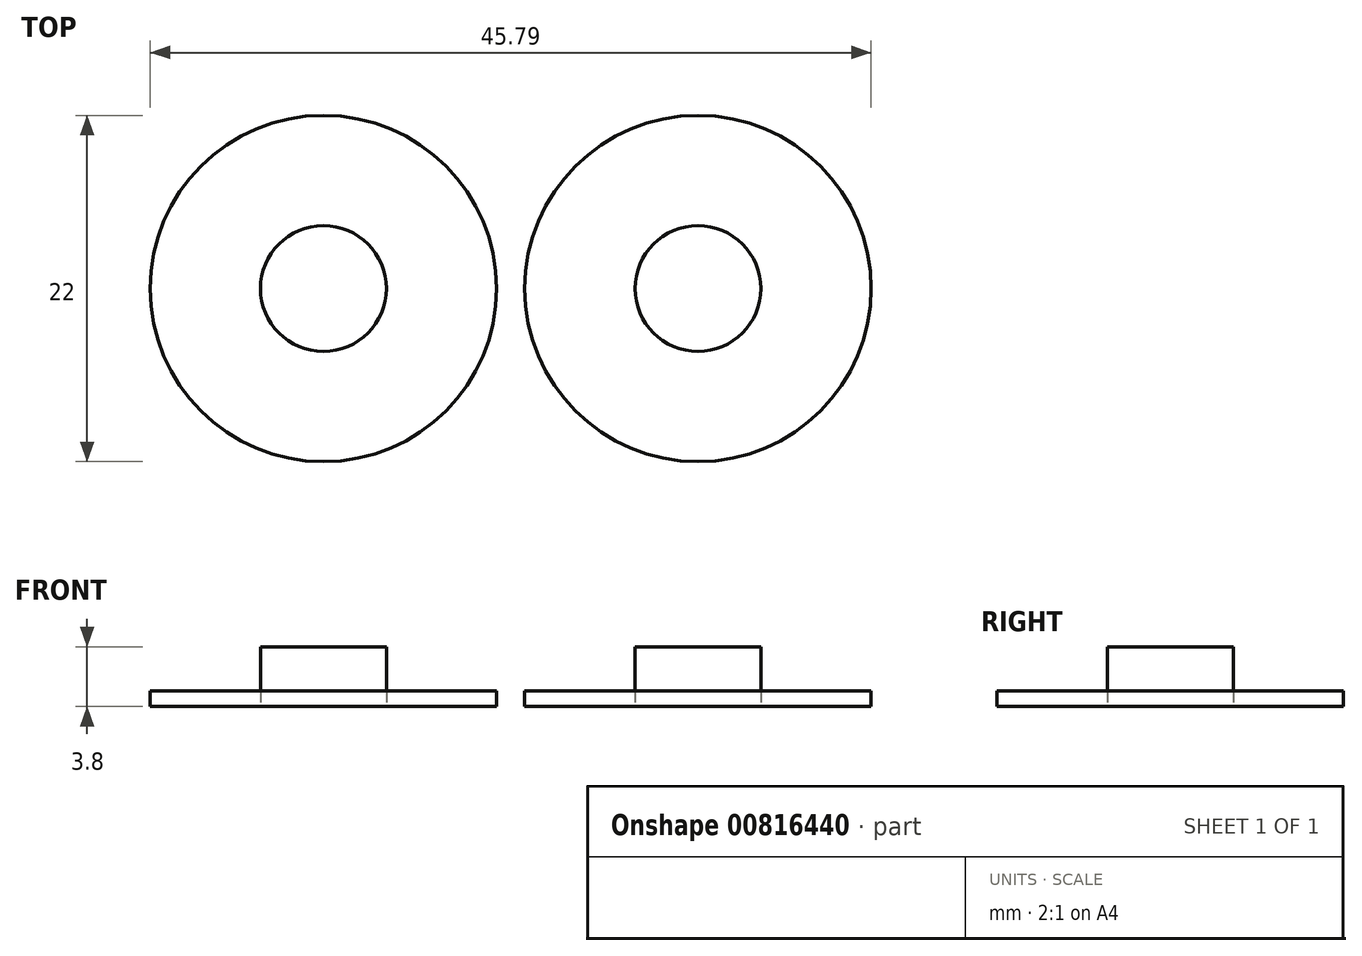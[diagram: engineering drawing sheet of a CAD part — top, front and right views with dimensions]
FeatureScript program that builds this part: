
annotation { "Feature Type Name" : "Feature", "Feature Type Description" : "" }
export const myFeature = defineFeature(function(context is Context, id is Id, definition is map)
    precondition{}
    {
        {
            var Q0;
            Q0=qCreatedBy(makeId("Top.planeOp"),FACE);
            var sketch = newSketch(context, id + "F0", { "sketchPlane" : qUnion([Q0])});
            skCircle(sketch, "E0", {"center": v(0, 0) * mm, "radius": 11 * mm});
            skCircle(sketch, "E1", {"center": v(0, 0) * mm, "radius": 4 * mm});
            skCircle(sketch, "E2", {"center": v(23.79, 0) * mm, "radius": 11 * mm});
            skCircle(sketch, "E3", {"center": v(23.79, 0) * mm, "radius": 4 * mm});
            skSolve(sketch);
        }
        {
            var Q0;
            Q0=makeQuery(id+"F0.imprint","IMPRINT",FACE,{"disambiguationData":[TD([[makeQuery(id+"F0.imprint","IMPRINT",EDGE,{"derivedFrom":sQuery(id+"F0.wireOp",EDGE,"E3")}),1.0]])]});
            var Q1;
            Q1=makeQuery(id+"F0.imprint","IMPRINT",FACE,{"disambiguationData":[TD([[makeQuery(id+"F0.imprint","IMPRINT",EDGE,{"derivedFrom":sQuery(id+"F0.wireOp",EDGE,"E2")}),1.0]])]});
            var Q2;
            Q2=makeQuery(id+"F0.imprint","IMPRINT",FACE,{"disambiguationData":[TD([[makeQuery(id+"F0.imprint","IMPRINT",EDGE,{"derivedFrom":sQuery(id+"F0.wireOp",EDGE,"E0")}),1.0]])]});
            var Q3;
            Q3=makeQuery(id+"F0.imprint","IMPRINT",FACE,{"disambiguationData":[TD([[makeQuery(id+"F0.imprint","IMPRINT",EDGE,{"derivedFrom":sQuery(id+"F0.wireOp",EDGE,"E1")}),1.0]])]});
            extrude(context, id + "F1", {"entities" : qUnion([Q0, Q1, Q2, Q3]), "depth" : 1 * mm, "offsetDistance" : 25.4 * mm});
        }
        {
            var Q0;
            Q0=makeQuery(id+"F0.imprint","IMPRINT",FACE,{"disambiguationData":[TD([[makeQuery(id+"F0.imprint","IMPRINT",EDGE,{"derivedFrom":sQuery(id+"F0.wireOp",EDGE,"E1")}),1.0]])]});
            var Q1;
            Q1=makeQuery(id+"F0.imprint","IMPRINT",FACE,{"disambiguationData":[TD([[makeQuery(id+"F0.imprint","IMPRINT",EDGE,{"derivedFrom":sQuery(id+"F0.wireOp",EDGE,"E3")}),1.0]])]});
            extrude(context, id + "F2", {"entities" : qUnion([Q0, Q1]), "depth" : 3.8 * mm, "offsetDistance" : 25.4 * mm});
        }
    });
